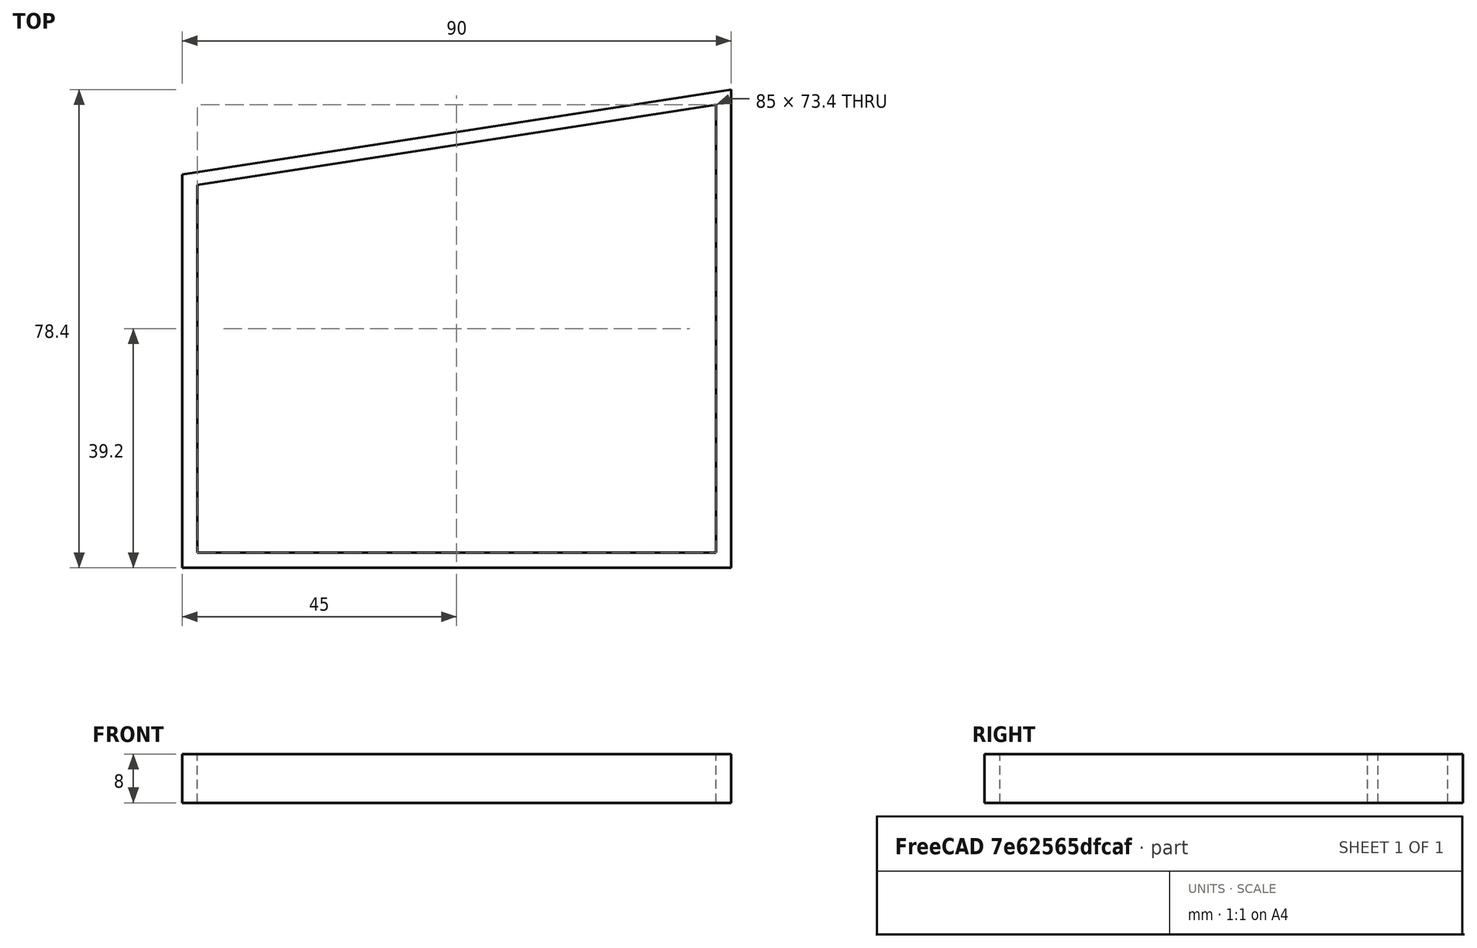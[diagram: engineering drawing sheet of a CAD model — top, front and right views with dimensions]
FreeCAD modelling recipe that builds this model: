
FCSTD DOCUMENT  (FreeCAD 1.0R39109 (Git))
Label: Gerüst-Fuß-V2.0-links-DerGerät
License: All rights reserved
LicenseURL: https://en.wikipedia.org/wiki/All_rights_reserved
objects: Sketcher::SketchObject×1, PartDesign::Pad×1, PartDesign::Body×1
note: 6 computed .brp shape members not serialized (recipe doc carries the construction recipe); baked Part::Feature solids carry a one-line shape summary decoded from their .brp

FEATURE [Sketcher::SketchObject] Sketch
  ArcFitTolerance = 1e-06
  AttachmentSupport = -> [XY_Plane]
  FullyConstrained = true
  MakeInternals = false
  MapMode = 5
  sketch-geometry (8):
    g0: LineSegment StartX=0 StartY=0 StartZ=0 EndX=0 EndY=64.5 EndZ=0
    g1: LineSegment StartX=0 StartY=64.5 StartZ=0 EndX=90 EndY=78.4 EndZ=0
    g2: LineSegment StartX=90 StartY=78.4 StartZ=0 EndX=90 EndY=0 EndZ=0
    g3: LineSegment StartX=90 StartY=0 StartZ=0 EndX=0 EndY=0 EndZ=0
    g4: LineSegment StartX=2.5 StartY=2.5 StartZ=0 EndX=87.5 EndY=2.5 EndZ=0
    g5: LineSegment StartX=87.5 StartY=2.5 StartZ=0 EndX=87.5 EndY=75.9 EndZ=0
    g6: LineSegment StartX=87.5 StartY=75.9 StartZ=0 EndX=2.5 EndY=62.7722 EndZ=0
    g7: LineSegment StartX=2.5 StartY=62.7722 StartZ=0 EndX=2.5 EndY=2.5 EndZ=0
  constraints (23):
    c: Coincident(g-1,g0)
    c: PointOnObject(g0,g-2)
    c: Coincident(g0,g1)
    c: Coincident(g1,g2)
    c: PointOnObject(g2,g-1)
    c: Vertical(g2)
    c: Coincident(g2,g3)
    c: Coincident(g3,g0)
    c: DistanceX(g3,g3) = 90
    c: DistanceY(g0,g0) = 64.5
    c: DistanceY(g2,g2) = 78.4
    c: Horizontal(g4)
    c: Coincident(g4,g5)
    c: Vertical(g5)
    c: Coincident(g5,g6)
    c: Coincident(g6,g7)
    c: Coincident(g7,g4)
    c: Vertical(g7)
    c: Distance(g0,g7) = 2.5
    c: Parallel(g1,g6)
    c: Distance(g2,g5) = 2.5
    c: DistanceY(g5,g5) = 73.4
    c: Distance(g3,g4) = 2.5
FEATURE [PartDesign::Pad] Pad
  Direction = (0,0,1)
  Length = 8
  Length2 = 10
  Profile = -> Sketch
  ReferenceAxis = -> Sketch [N_Axis]
  Refine = true
  Suppressed = false
  Type = 0
FEATURE [PartDesign::Body] Body  label="Körper"
  AllowCompound = false
  Group = -> [Sketch,Pad]
  Origin = -> Origin
  Tip = -> Pad
